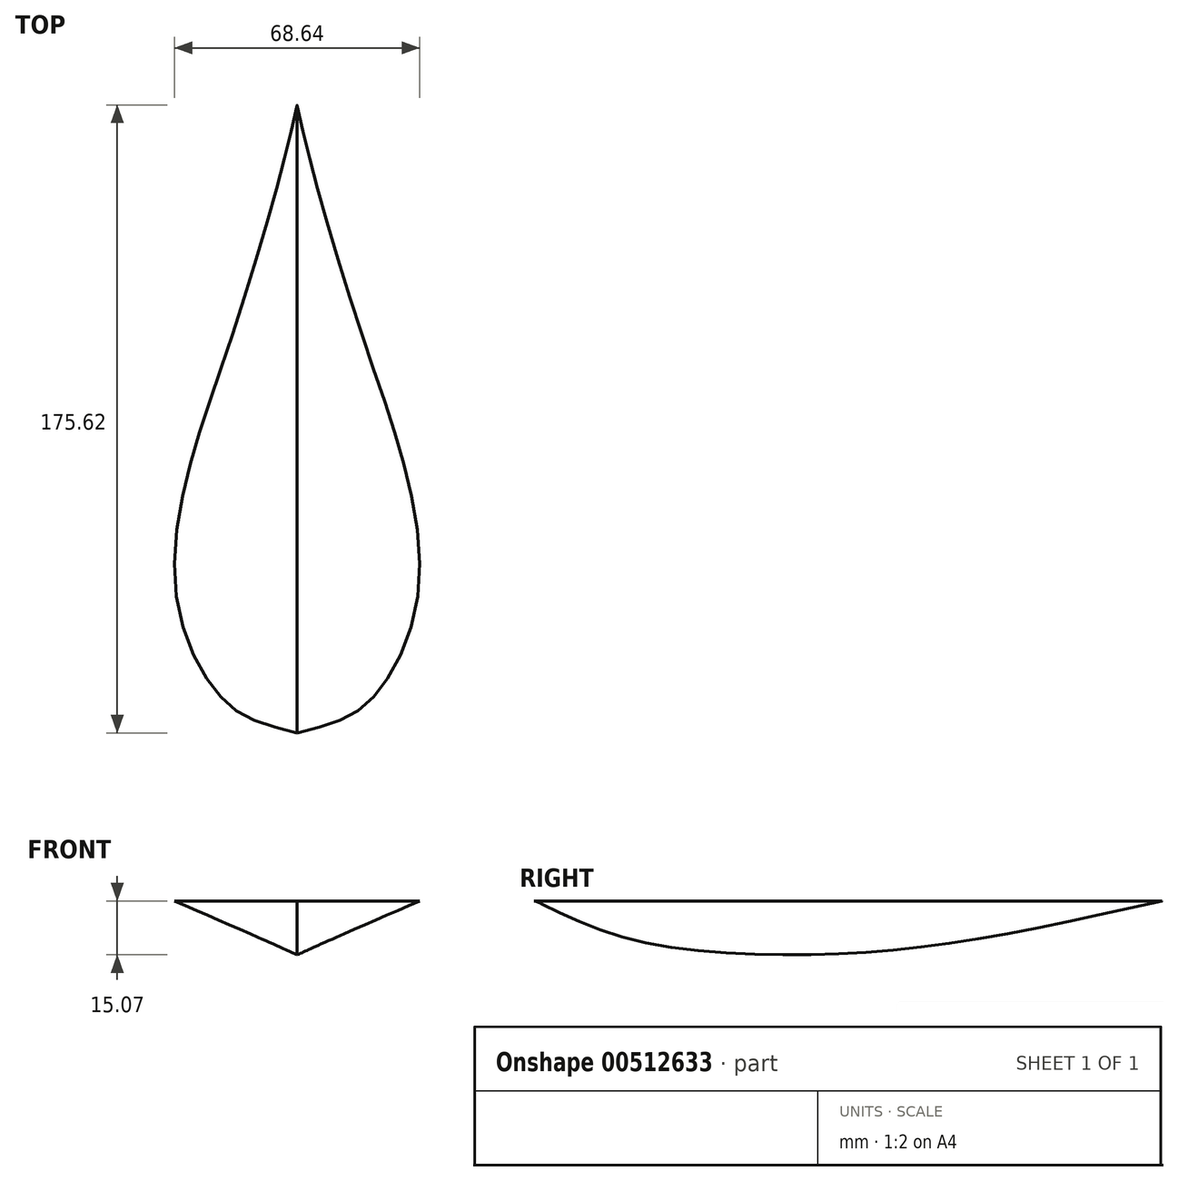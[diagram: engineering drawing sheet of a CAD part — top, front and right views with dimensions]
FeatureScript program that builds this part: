
annotation { "Feature Type Name" : "Feature", "Feature Type Description" : "" }
export const myFeature = defineFeature(function(context is Context, id is Id, definition is map)
    precondition{}
    {
        {
            var Q0;
            Q0=qCreatedBy(makeId("Right.planeOp"),FACE);
            var sketch = newSketch(context, id + "F0", { "sketchPlane" : qUnion([Q0])});
            skFitSpline(sketch, "E0", {"points": [v(-84.14, 0) * mm, v(-57.2, -10.81) * mm, v(-12.5, -15.07) * mm, v(33.95, -11.52) * mm, v(91.04, 0) * mm], "startDerivative": vector(122.08, -60.47) * mm, "endDerivative": vector(204.3, 45.92) * mm});
            skSolve(sketch);
        }
        {
            var Q0;
            Q0=qCreatedBy(makeId("Top.planeOp"),FACE);
            var sketch = newSketch(context, id + "F1", { "sketchPlane" : qUnion([Q0])});
            skFitSpline(sketch, "E1", {"points": [v(0, -84.58) * mm, v(-14.36, -79.97) * mm, v(-24.65, -70.4) * mm, v(-33.87, -45.92) * mm, v(-30.32, -11.17) * mm, v(-19.68, 22.16) * mm, v(-6.2, 65.78) * mm, v(0, 90.96) * mm], "startDerivative": vector(-143.13, 34.1) * mm, "endDerivative": vector(37.67, 164.96) * mm});
            skSolve(sketch);
        }
        {
            var Q0;
            Q0=sQuery(id+"F1.wireOp",EDGE,"E1");
            var Q1;
            Q1=sQuery(id+"F0.wireOp",EDGE,"E0");
            loft(context, id + "F2", {"bodyType" : ToolBodyType.SURFACE, "wireProfilesArray" : [{ "wireProfileEntities" : qUnion([Q0]) }, { "wireProfileEntities" : qUnion([Q1]) }]});
        }
        {
            var Q0;
            Q0=makeQuery(id+"F2.opLoft","SWEPT_BODY",BODY,{"disambiguationData":[OSD([sQuery(id+"F0.wireOp",EDGE,"E0"),sQuery(id+"F1.wireOp",EDGE,"E1")])]});
            var Q1;
            Q1=qCreatedBy(makeId("Right.planeOp"),FACE);
            mirror(context, id + "F3", {"entities" : qUnion([Q0]), "mirrorPlane" : qUnion([Q1])});
        }
    });
